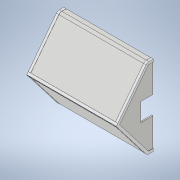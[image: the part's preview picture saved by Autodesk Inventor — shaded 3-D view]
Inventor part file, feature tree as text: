
AUTODESK INVENTOR PART (.ipt)
format: ipt  version: 2021 (Build 250183000, 183)  size: 154,112 bytes
history: imported  units: in
note: dims shown in document units (in); Inventor stores cm internally (conversion verified against a paired STEP export)
features: imported_body x1
ambient origin geometry x8: Origin, YZ Plane, XZ Plane, XY Plane, X Axis, Y Axis, Z Axis, Center Point
bodies: Solid1 (imported_parasolid), Body2 (imported_parasolid)
feature tree (1):
  imported_body  NMx_Import_Brep_tag  [imported B-rep: ~49 faces, bbox_mm=[7300.0, 6520.0, 3015.85248]]
